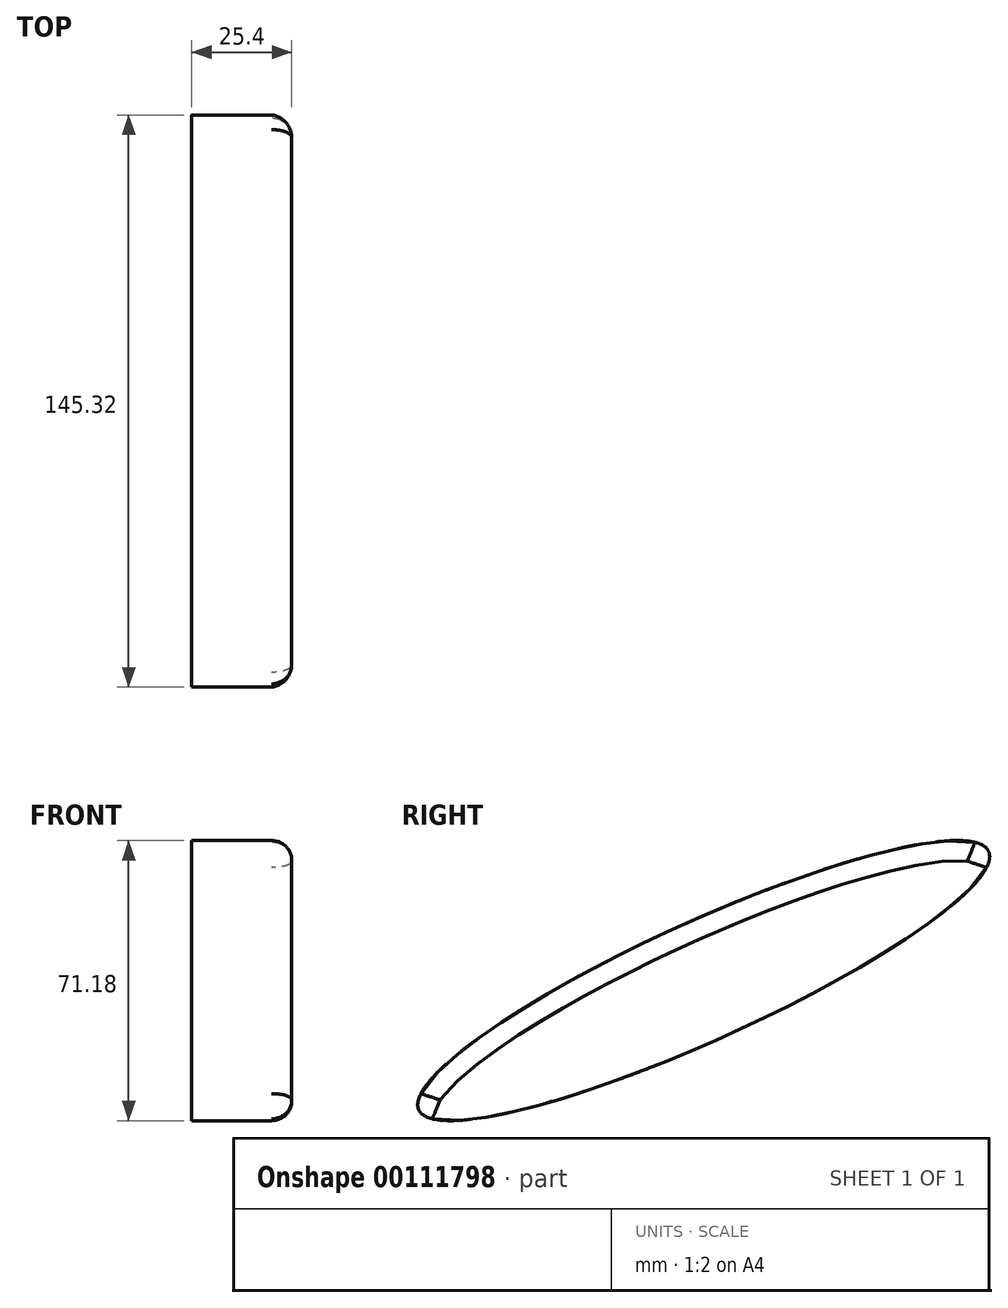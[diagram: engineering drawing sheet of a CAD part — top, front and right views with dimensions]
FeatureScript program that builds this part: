
annotation { "Feature Type Name" : "Feature", "Feature Type Description" : "" }
export const myFeature = defineFeature(function(context is Context, id is Id, definition is map)
    precondition{}
    {
        {
            var Q0;
            Q0=qCreatedBy(makeId("Right.planeOp"),FACE);
            var sketch = newSketch(context, id + "F0", { "sketchPlane" : qUnion([Q0])});
            skEllipse(sketch, "E0", {"center": v(0, 0) * mm, "majorRadius": 79.49 * mm, "minorRadius": 15.1 * mm, "majorAxis": v(0.91, 0.41)});
            skSolve(sketch);
        }
        {
            var Q0;
            Q0 = qSketchRegion(id + "F0", true);
            extrude(context, id + "F1", {"entities" : qUnion([Q0]), "depth" : 25.4 * mm});
        }
        {
            var Q0;
            Q0=makeQuery(id+"F1.opExtrude","CAP_EDGE",EDGE,{"disambiguationData":[OSD([sQuery(id+"F0.wireOp",EDGE,"E0")])],"isStart":false});
            fillet(context, id + "F2", {"entities" : qUnion([Q0]), "radius" : 5.08 * mm, "tangentPropagation" : true, "allowEdgeOverflow" : false});
        }
    });
